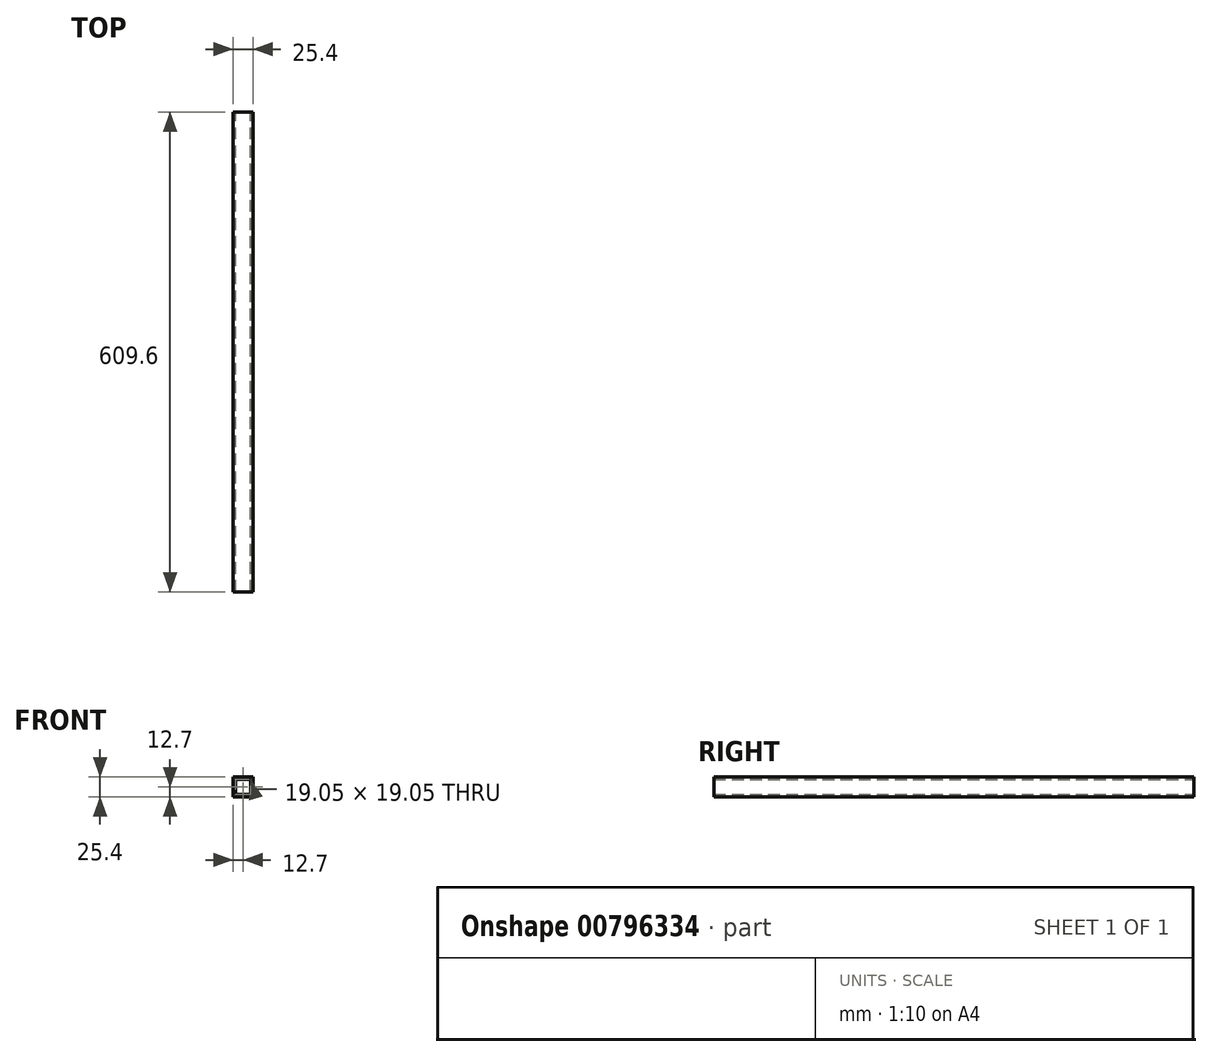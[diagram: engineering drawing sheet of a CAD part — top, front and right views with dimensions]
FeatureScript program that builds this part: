
annotation { "Feature Type Name" : "Feature", "Feature Type Description" : "" }
export const myFeature = defineFeature(function(context is Context, id is Id, definition is map)
    precondition{}
    {
        {
            var Q0;
            Q0=qCreatedBy(makeId("Front.planeOp"),FACE);
            var sketch = newSketch(context, id + "F0", { "sketchPlane" : qUnion([Q0])});
            skLineSegment(sketch, "E0.bottom", {"start": v(-12.7, 12.7) * mm, "end": v(12.7, 12.7) * mm});
            skLineSegment(sketch, "E0.top", {"start": v(-12.7, -12.7) * mm, "end": v(12.7, -12.7) * mm});
            skLineSegment(sketch, "E0.left", {"start": v(-12.7, 12.7) * mm, "end": v(-12.7, -12.7) * mm});
            skLineSegment(sketch, "E0.right", {"start": v(12.7, 12.7) * mm, "end": v(12.7, -12.7) * mm});
            skPoint(sketch, "E0.middle", {"position": v(0, 0) * mm});
            skLineSegment(sketch, "E1.bottom", {"start": v(-9.52, 9.52) * mm, "end": v(9.53, 9.52) * mm});
            skLineSegment(sketch, "E1.top", {"start": v(-9.53, -9.52) * mm, "end": v(9.52, -9.52) * mm});
            skLineSegment(sketch, "E1.left", {"start": v(-9.52, 9.52) * mm, "end": v(-9.53, -9.52) * mm});
            skLineSegment(sketch, "E1.right", {"start": v(9.53, 9.52) * mm, "end": v(9.52, -9.52) * mm});
            skSolve(sketch);
        }
        {
            var Q0;
            Q0=makeQuery(id+"F0.imprint","IMPRINT",FACE,{"disambiguationData":[TD([[makeQuery(id+"F0.imprint","IMPRINT",EDGE,{"derivedFrom":sQuery(id+"F0.wireOp",EDGE,"E0.bottom")}),-1.0]])]});
            extrude(context, id + "F1", {"entities" : qUnion([Q0]), "depth" : 609.6 * mm, "offsetDistance" : 25.4 * mm});
        }
    });
